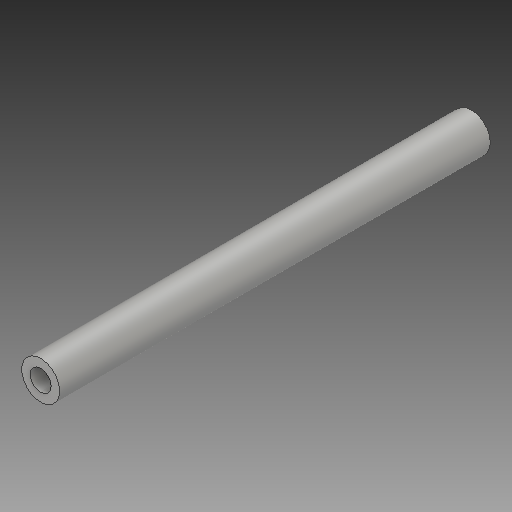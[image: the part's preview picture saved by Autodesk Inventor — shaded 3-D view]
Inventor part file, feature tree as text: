
AUTODESK INVENTOR PART (.ipt)
format: ipt  version: 2019 (Build 230136000, 136)  size: 94,208 bytes
history: native  units: mm
features: extrude x1, sketch x1
ambient origin geometry x8: Origin, YZ Plane, XZ Plane, XY Plane, X Axis, Y Axis, Z Axis, Center Point
bodies: Solid1 (feature_tree)
feature tree (2):
  extrude  "Extrusion1"  Depth=136.0mm
  sketch  "Sketch1"  dims[d0=12.0mm d1=6.6mm d2=136.0mm d3=0.0mm]
